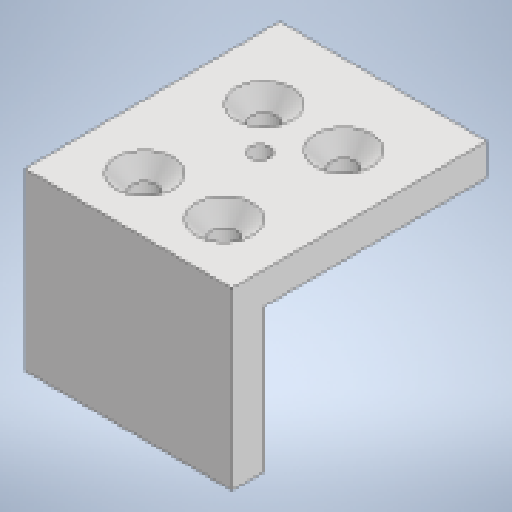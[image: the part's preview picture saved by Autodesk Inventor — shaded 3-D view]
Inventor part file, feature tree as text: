
AUTODESK INVENTOR PART (.ipt)
format: ipt  version: 2024.1 (Build 281209000, 209)  size: 182,784 bytes
history: native  units: in
note: dims shown in document units (in); Inventor stores cm internally (conversion verified against a paired STEP export)
features: sketch x6, extrude x5, chamfer x1
ambient origin geometry x8: Origin, YZ Plane, XZ Plane, XY Plane, X Axis, Y Axis, Z Axis, Center Point
bodies: Solid1 (feature_tree)
feature tree (12):
  extrude  "Extrusion1"  Depth=1.0236in
  extrude  "Extrusion2"  Depth=0.1575in
  sketch  "Sketch3"  dims[d5=0.122in d6=0.122in]
  extrude  "Extrusion3"  Depth=0.122in
  chamfer  "Chamfer1"  Distance=0.5906in
  extrude  "Extrusion4"  Depth=0.9843in
  extrude  "Extrusion5"  Depth=0.1969in
  sketch  "Sketch1"  dims[d0=1.0236in d1=1.1811in]
  sketch  "Sketch2"  dims[d2=0.1575in d3=0.0in d4=0.122in]
  sketch  "Sketch4"  dims[d7=0.122in]
  sketch  "Sketch5"  dims[d8=0.3937in]
  sketch  "Sketch6"  dims[d9=0.3937in d10=0.5906in d11=0.5906in d12=0.1969in d13=0.1969in d14=0.315in d15=0.315in d16=0.0in d17=0.0in d18=0.0787in d19=0.1575in d20=0.8661in d21=0.3937in d22=0.0in d23=0.0787in d24=0.0787in d25=45.0deg d26=0.0984in d27=0.6102in d28=0.5118in d29=0.0in d30=0.0in d31=0.1969in d32=0.9843in d33=0.0in]
